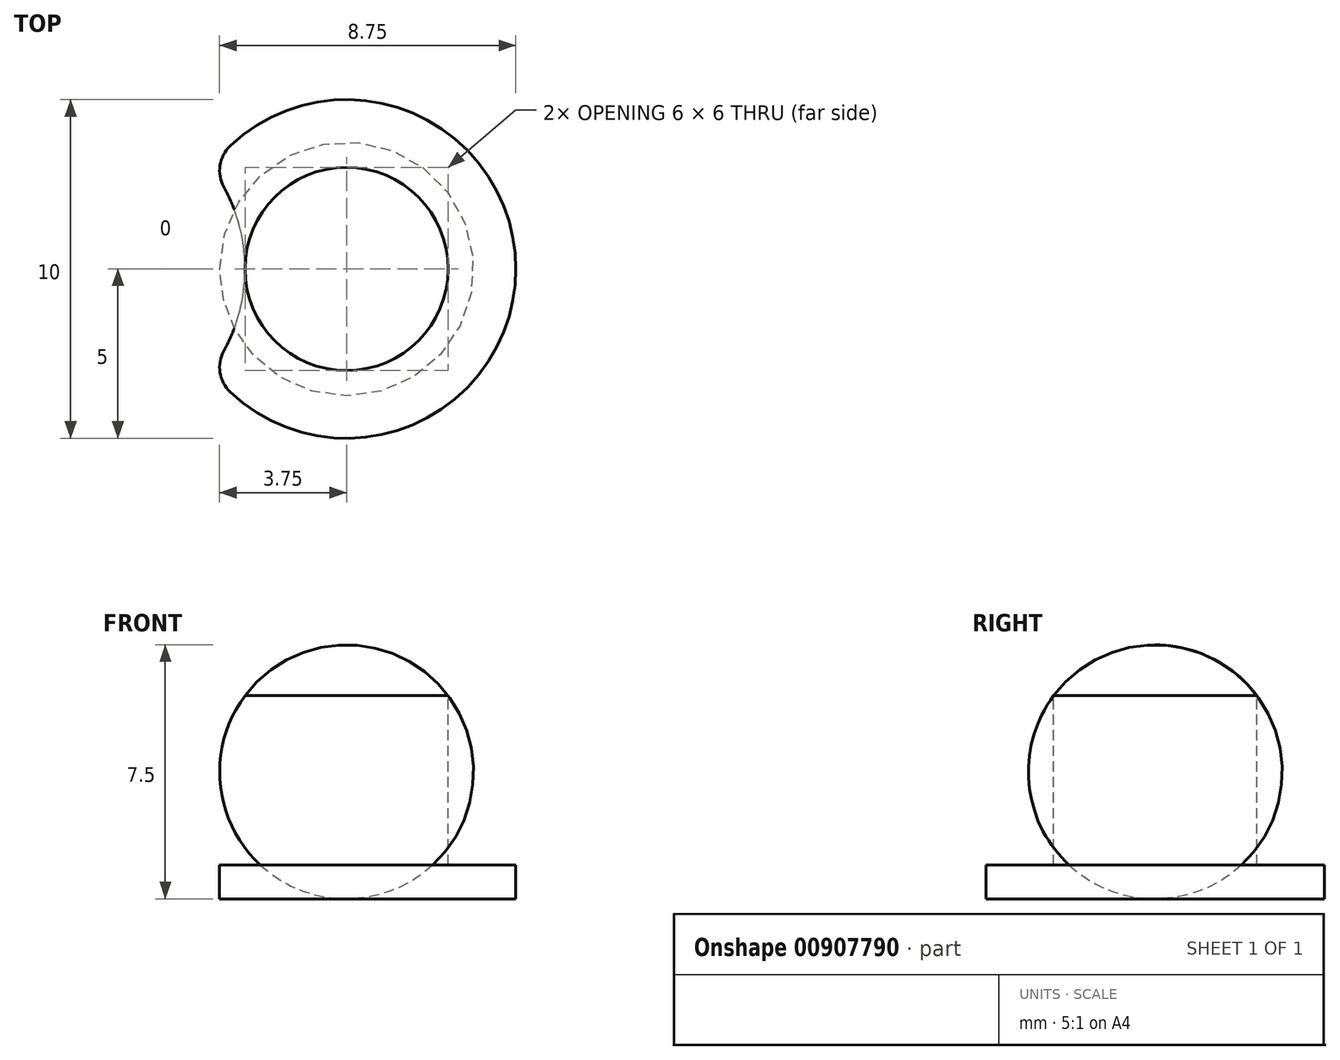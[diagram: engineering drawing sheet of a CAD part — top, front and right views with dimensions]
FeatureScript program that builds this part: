
annotation { "Feature Type Name" : "Feature", "Feature Type Description" : "" }
export const myFeature = defineFeature(function(context is Context, id is Id, definition is map)
    precondition{}
    {
        {
            var Q0;
            Q0=qCreatedBy(makeId("Front.planeOp"),FACE);
            var sketch = newSketch(context, id + "F0", { "sketchPlane" : qUnion([Q0])});
            skLineSegment(sketch, "E0.bottom", {"start": v(0, 0) * mm, "end": v(3, 0) * mm});
            skLineSegment(sketch, "E0.top", {"start": v(0, -5) * mm, "end": v(3, -5) * mm});
            skLineSegment(sketch, "E0.left", {"start": v(0, 0) * mm, "end": v(0, -5) * mm});
            skLineSegment(sketch, "E0.right", {"start": v(3, 0) * mm, "end": v(3, -5) * mm});
            skLineSegment(sketch, "E1", {"start": v(0, 0) * mm, "end": v(0, 1.5) * mm});
            skArc(sketch, "E2.trimOffspring", {"start": v(3, 0) * mm, "mid": v(1.68, 1.1) * mm, "end": v(0, 1.5) * mm});
            skLineSegment(sketch, "E3.bottom", {"start": v(0, -5) * mm, "end": v(5, -5) * mm});
            skLineSegment(sketch, "E3.top", {"start": v(0, -6) * mm, "end": v(5, -6) * mm});
            skLineSegment(sketch, "E3.left", {"start": v(0, -5) * mm, "end": v(0, -6) * mm});
            skLineSegment(sketch, "E3.right", {"start": v(5, -5) * mm, "end": v(5, -6) * mm});
            skSolve(sketch);
        }
        {
            var Q0;
            Q0=makeQuery(id+"F0.imprint","IMPRINT",FACE,{"disambiguationData":[TD([[makeQuery(id+"F0.imprint","IMPRINT",EDGE,{"derivedFrom":sQuery(id+"F0.wireOp",EDGE,"E0.bottom")}),1.0]])]});
            var Q1;
            Q1=makeQuery(id+"F0.imprint","IMPRINT",FACE,{"disambiguationData":[TD([[makeQuery(id+"F0.imprint","IMPRINT",EDGE,{"derivedFrom":sQuery(id+"F0.wireOp",EDGE,"E0.bottom")}),-1.0]])]});
            var Q2;
            Q2=makeQuery(id+"F0.imprint","IMPRINT",FACE,{"disambiguationData":[TD([[makeQuery(id+"F0.imprint","IMPRINT",EDGE,{"derivedFrom":sQuery(id+"F0.wireOp",EDGE,"E3.top")}),1.0]])]});
            var Q3;
            Q3=sQuery(id+"F0.wireOp",EDGE,"E0.left");
            revolve(context, id + "F1", {"surfaceOperationType" : NewSurfaceOperationType.NEW, "entities" : qUnion([Q0, Q1, Q2]), "axis" : qUnion([Q3]), "revolveType" : RevolveType.FULL});
        }
        {
            var Q0;
            Q0=makeQuery(id+"F1.opRevolve","SWEPT_FACE",FACE,{"disambiguationData":[OSD([sQuery(id+"F0.wireOp",EDGE,"E3.bottom")])]});
            var sketch = newSketch(context, id + "F2", { "sketchPlane" : qUnion([Q0])});
            skPoint(sketch, "E4", {"position": v(-3, 0) * mm});
            skCircle(sketch, "E5", {"center": v(-8, 0) * mm, "radius": 5 * mm});
            skSolve(sketch);
        }
        {
            var Q0;
            Q0 = qSketchRegion(id + "F2", true);
            extrude(context, id + "F3", {"entities" : qUnion([Q0]), "operationType" : NewBodyOperationType.REMOVE, "oppositeDirection" : true, "depth" : 25 * mm, "offsetDistance" : 25 * mm});
        }
        {
            var Q0;
            Q0=makeQuery(id+"F3.boolean.opBoolean","INTERSECT",EDGE,{"disambiguationData":[OD(1.0)],"derivedFrom":[makeQuery(id+"F1.opRevolve","SWEPT_FACE",FACE,{"disambiguationData":[OSD([sQuery(id+"F0.wireOp",EDGE,"E3.right")])]}),makeQuery(id+"F3.opExtrude","SWEPT_FACE",FACE,{"disambiguationData":[OSD([sQuery(id+"F2.wireOp",EDGE,"E5")])]})]});
            var Q1;
            Q1=makeQuery(id+"F3.boolean.opBoolean","INTERSECT",EDGE,{"disambiguationData":[OD(0.0)],"derivedFrom":[makeQuery(id+"F1.opRevolve","SWEPT_FACE",FACE,{"disambiguationData":[OSD([sQuery(id+"F0.wireOp",EDGE,"E3.right")])]}),makeQuery(id+"F3.opExtrude","SWEPT_FACE",FACE,{"disambiguationData":[OSD([sQuery(id+"F2.wireOp",EDGE,"E5")])]})]});
            fillet(context, id + "F4", {"entities" : qUnion([Q0, Q1]), "radius" : 1 * mm, "tangentPropagation" : true, "allowEdgeOverflow" : false});
        }
    });
